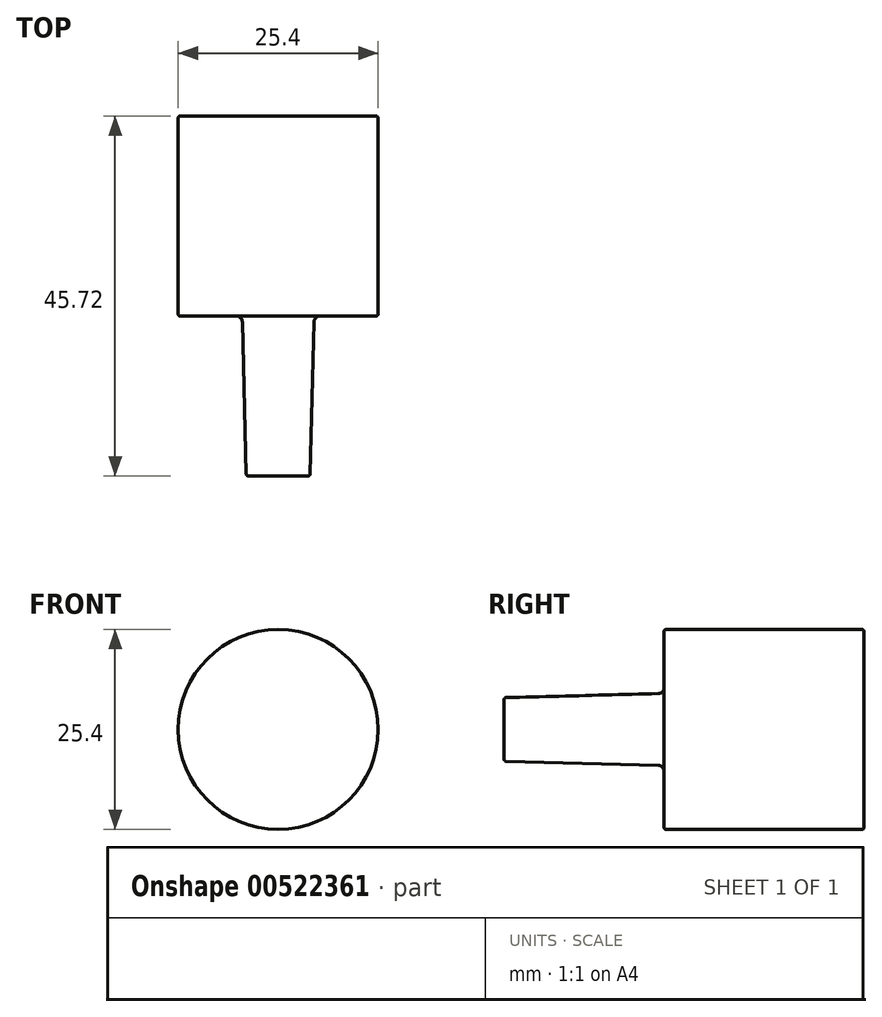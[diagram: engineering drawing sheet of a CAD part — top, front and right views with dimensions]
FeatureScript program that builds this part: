
annotation { "Feature Type Name" : "Feature", "Feature Type Description" : "" }
export const myFeature = defineFeature(function(context is Context, id is Id, definition is map)
    precondition{}
    {
        {
            var Q0;
            Q0=qCreatedBy(makeId("Right.planeOp"),FACE);
            var sketch = newSketch(context, id + "F0", { "sketchPlane" : qUnion([Q0])});
            skLineSegment(sketch, "E0", {"start": v(25.4, 0) * mm, "end": v(25.4, 12.7) * mm});
            skLineSegment(sketch, "E1", {"start": v(25.4, 12.7) * mm, "end": v(0, 12.7) * mm});
            skLineSegment(sketch, "E2", {"start": v(0, 12.7) * mm, "end": v(0, 4.57) * mm});
            skLineSegment(sketch, "E3", {"start": v(0, 4.57) * mm, "end": v(-20.32, 4.04) * mm});
            skLineSegment(sketch, "E4", {"start": v(-20.32, 4.04) * mm, "end": v(-20.32, 0) * mm});
            skLineSegment(sketch, "E5", {"start": v(-20.32, 0) * mm, "end": v(25.4, 0) * mm});
            skLineSegment(sketch, "E6", {"start": v(-47.9, 0) * mm, "end": v(43.15, 0) * mm, "construction": true});
            skSolve(sketch);
        }
        {
            var Q0;
            Q0=qSketchRegion(id+"F0",true);
            var Q1;
            Q1=sQuery(id+"F0.wireOp",EDGE,"E5");
            revolve(context, id + "F1", {"entities" : qUnion([Q0]), "axis" : qUnion([Q1]), "revolveType" : RevolveType.FULL});
        }
        {
            var Q0;
            Q0=makeQuery(id+"F1.opRevolve","SWEPT_EDGE",EDGE,{"disambiguationData":[OSD([sQuery(id+"F0.wireOp",EDGE,"E2"),sQuery(id+"F0.wireOp",EDGE,"E3")])]});
            fillet(context, id + "F2", {"entities" : qUnion([Q0]), "radius" : 0.76 * mm, "tangentPropagation" : true, "allowEdgeOverflow" : false});
        }
        {
            var Q0;
            Q0=makeQuery(id+"F1.opRevolve","SWEPT_EDGE",EDGE,{"disambiguationData":[OSD([sQuery(id+"F0.wireOp",EDGE,"E1"),sQuery(id+"F0.wireOp",EDGE,"E2")])]});
            var Q1;
            Q1=makeQuery(id+"F1.opRevolve","SWEPT_EDGE",EDGE,{"disambiguationData":[OSD([sQuery(id+"F0.wireOp",EDGE,"E0"),sQuery(id+"F0.wireOp",EDGE,"E1")])]});
            var Q2;
            Q2=makeQuery(id+"F1.opRevolve","SWEPT_EDGE",EDGE,{"disambiguationData":[OSD([sQuery(id+"F0.wireOp",EDGE,"E3"),sQuery(id+"F0.wireOp",EDGE,"E4")])]});
            fillet(context, id + "F3", {"entities" : qUnion([Q0, Q1, Q2]), "radius" : 0.25 * mm, "tangentPropagation" : true, "allowEdgeOverflow" : false});
        }
    });
